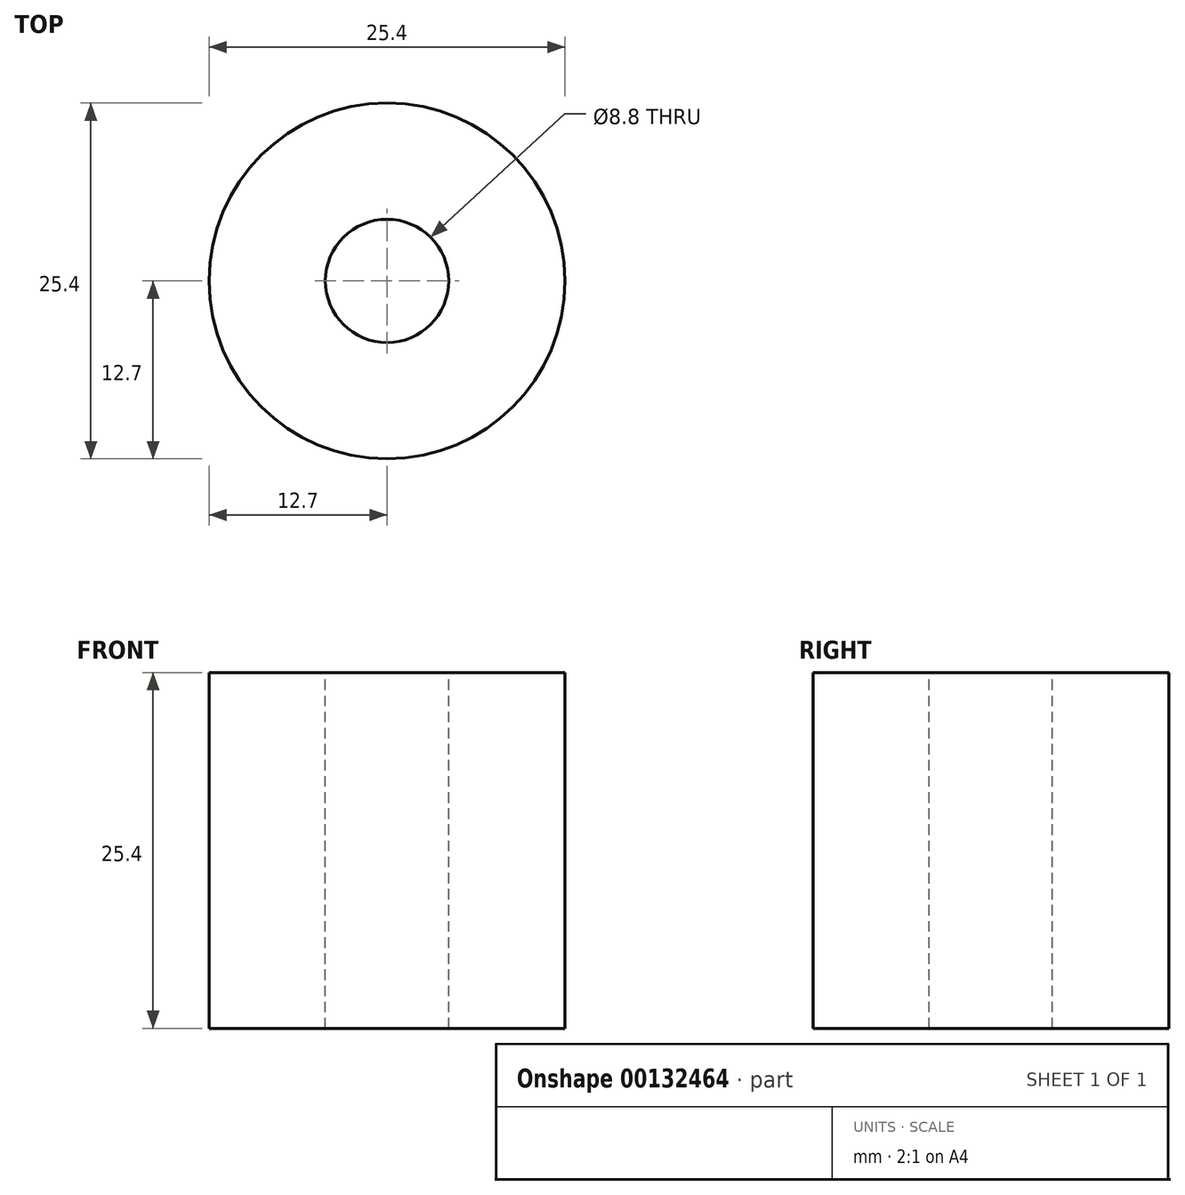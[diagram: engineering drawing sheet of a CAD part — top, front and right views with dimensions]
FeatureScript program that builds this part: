
annotation { "Feature Type Name" : "Feature", "Feature Type Description" : "" }
export const myFeature = defineFeature(function(context is Context, id is Id, definition is map)
    precondition{}
    {
        {
            var Q0;
            Q0=qCreatedBy(makeId("Top.planeOp"),FACE);
            var sketch = newSketch(context, id + "F0", { "sketchPlane" : qUnion([Q0])});
            skCircle(sketch, "E0", {"center": v(0, 0) * mm, "radius": 12.7 * mm});
            skSolve(sketch);
        }
        {
            var Q0;
            Q0=makeQuery(id+"F0.imprint","IMPRINT",FACE,{"disambiguationData":[TD([[makeQuery(id+"F0.imprint","IMPRINT",EDGE,{"derivedFrom":sQuery(id+"F0.wireOp",EDGE,"E0")}),1.0]])]});
            extrude(context, id + "F1", {"entities" : qUnion([Q0]), "depth" : 25.4 * mm});
        }
        {
            var Q0;
            Q0=makeQuery(id+"F1.opExtrude","CAP_FACE",FACE,{"disambiguationData":[OSD([sQuery(id+"F0.wireOp",EDGE,"E0")])],"isStart":false});
            var sketch = newSketch(context, id + "F2", { "sketchPlane" : qUnion([Q0])});
            skCircle(sketch, "E1", {"center": v(0, 0) * mm, "radius": 7.05 * mm});
            skSolve(sketch);
        }
        {
            var Q0;
            Q0=sQuery(id+"F2.wireOp",VERTEX,"E1.center");
            var Q1;
            Q1=makeQuery(id+"F1.opExtrude","SWEPT_BODY",BODY,{"disambiguationData":[OSD([sQuery(id+"F0.wireOp",EDGE,"E0")])]});
            hole(context, id + "F3", {"style" : HoleStyle.SIMPLE, "endStyle" : HoleEndStyle.THROUGH, "standardTappedOrClearance" : lookupTablePath({ "standard" : "ISO", "fit" : "Normal", "size" : "M8", "type" : "Clearance" }), "standardBlindInLast" : lookupTablePath({ "fit" : "Standard", "standard" : "ISO", "size" : "M8", "type" : "Clearance" }), "holeDiameter" : 8.8 * mm, "locations" : qUnion([Q0]), "scope" : qUnion([Q1]), "isTappedThrough" : true});
        }
    });
